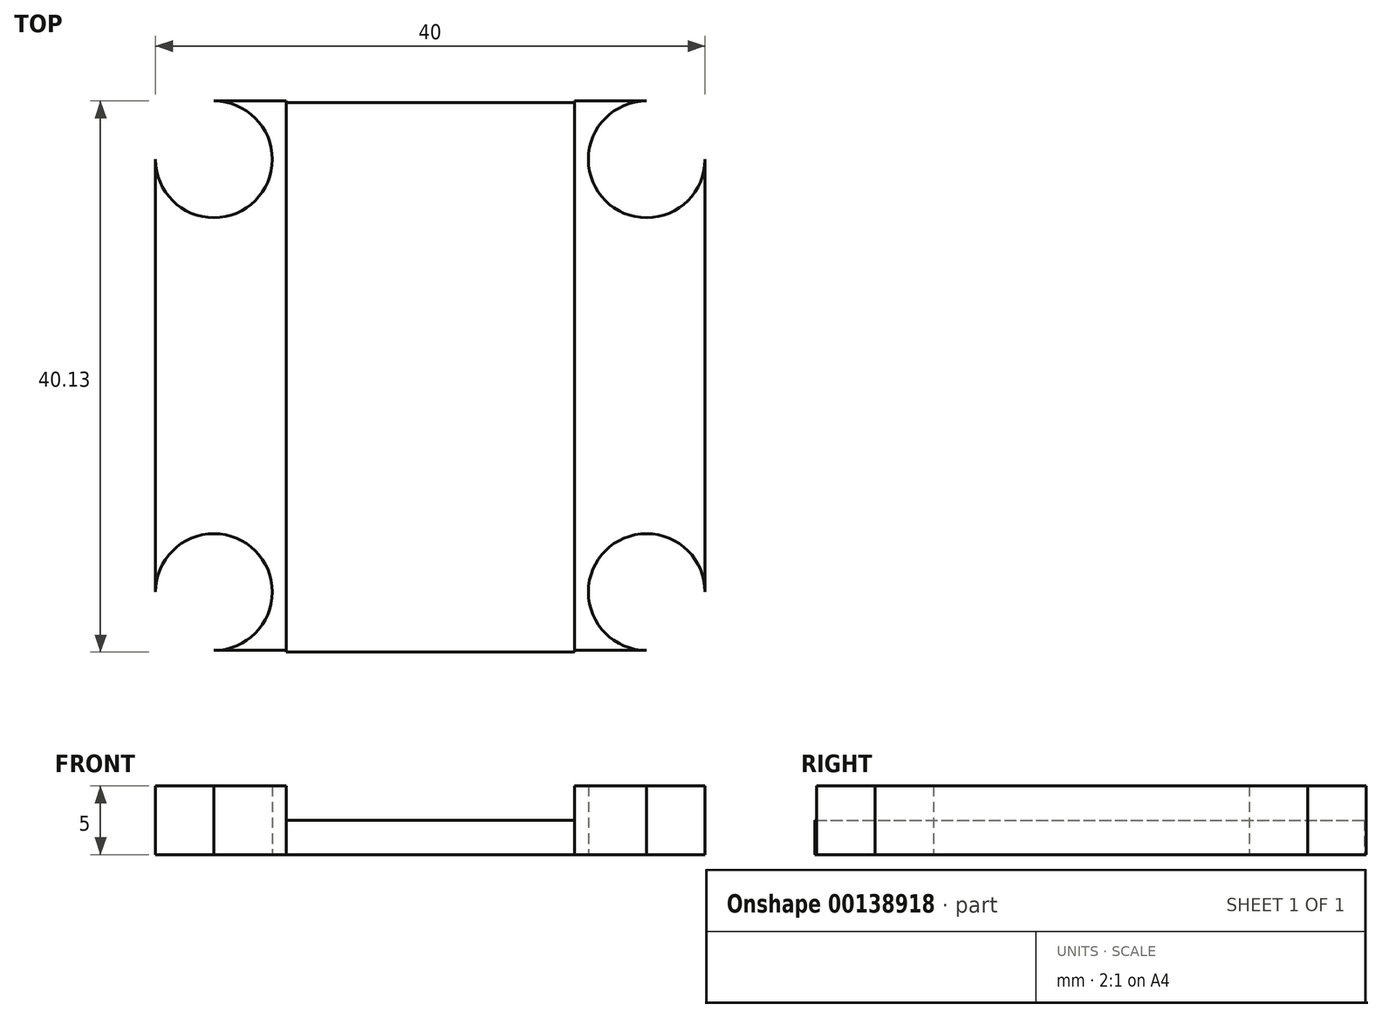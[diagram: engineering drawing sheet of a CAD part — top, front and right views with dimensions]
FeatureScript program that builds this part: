
annotation { "Feature Type Name" : "Feature", "Feature Type Description" : "" }
export const myFeature = defineFeature(function(context is Context, id is Id, definition is map)
    precondition{}
    {
        {
            var Q0;
            Q0=qCreatedBy(makeId("Top.planeOp"),FACE);
            var sketch = newSketch(context, id + "F0", { "sketchPlane" : qUnion([Q0])});
            skLineSegment(sketch, "E0.bottom", {"start": v(-32, 20.8) * mm, "end": v(8, 20.8) * mm});
            skLineSegment(sketch, "E0.top", {"start": v(-32, -19.2) * mm, "end": v(8, -19.2) * mm});
            skLineSegment(sketch, "E0.left", {"start": v(-32, 20.8) * mm, "end": v(-32, -19.2) * mm});
            skLineSegment(sketch, "E0.right", {"start": v(8, 20.8) * mm, "end": v(8, -19.2) * mm});
            skCircle(sketch, "E1", {"center": v(3.74, 16.55) * mm, "radius": 4.25 * mm});
            skCircle(sketch, "E2", {"center": v(-27.76, 16.55) * mm, "radius": 4.25 * mm});
            skCircle(sketch, "E3", {"center": v(3.74, -14.95) * mm, "radius": 4.25 * mm});
            skCircle(sketch, "E4", {"center": v(-27.76, -14.95) * mm, "radius": 4.25 * mm});
            skCircle(sketch, "E5", {"center": v(3.74, 16.55) * mm, "radius": 3.8 * mm});
            skCircle(sketch, "E6", {"center": v(3.74, -14.95) * mm, "radius": 3.8 * mm});
            skCircle(sketch, "E7", {"center": v(-27.76, 16.55) * mm, "radius": 3.8 * mm});
            skCircle(sketch, "E8", {"center": v(-27.76, -14.95) * mm, "radius": 3.8 * mm});
            skLineSegment(sketch, "E9.bottom", {"start": v(-22.5, -19.2) * mm, "end": v(-1.5, -19.2) * mm});
            skLineSegment(sketch, "E9.top", {"start": v(-22.5, 20.8) * mm, "end": v(-1.5, 20.8) * mm});
            skLineSegment(sketch, "E9.left", {"start": v(-22.5, -19.2) * mm, "end": v(-22.5, 20.8) * mm});
            skLineSegment(sketch, "E9.right", {"start": v(-1.5, -19.2) * mm, "end": v(-1.5, 20.8) * mm});
            skSolve(sketch);
        }
        {
            var Q0;
            {var subQ5=sQuery(id+"F0.wireOp",EDGE,"E9.left");Q0=makeQuery(id+"F0.imprint","IMPRINT",FACE,{"disambiguationData":[TD([[makeQuery(id+"F0.imprint","IMPRINT",EDGE,{"derivedFrom":subQ5}),1.0]])]});}
            var Q1;
            {var subQ7=sQuery(id+"F0.wireOp",EDGE,"E9.right");Q1=makeQuery(id+"F0.imprint","IMPRINT",FACE,{"disambiguationData":[TD([[makeQuery(id+"F0.imprint","IMPRINT",EDGE,{"derivedFrom":subQ7}),-1.0]])]});}
            extrude(context, id + "F1", {"entities" : qUnion([Q0, Q1]), "depth" : 5 * mm});
        }
        {
            var Q0;
            Q0=qCreatedBy(makeId("Top.planeOp"),FACE);
            var sketch = newSketch(context, id + "F2", { "sketchPlane" : qUnion([Q0])});
            skLineSegment(sketch, "E10.bottom", {"start": v(-1.5, -19.33) * mm, "end": v(-22.5, -19.33) * mm});
            skLineSegment(sketch, "E10.top", {"start": v(-1.5, 20.67) * mm, "end": v(-22.5, 20.67) * mm});
            skLineSegment(sketch, "E10.left", {"start": v(-1.5, -19.33) * mm, "end": v(-1.5, 20.67) * mm});
            skLineSegment(sketch, "E10.right", {"start": v(-22.5, -19.33) * mm, "end": v(-22.5, 20.67) * mm});
            skSolve(sketch);
        }
        {
            var Q0;
            Q0=makeQuery(id+"F2.imprint","IMPRINT",FACE,{"disambiguationData":[TD([[makeQuery(id+"F2.imprint","IMPRINT",EDGE,{"derivedFrom":sQuery(id+"F2.wireOp",EDGE,"E10.bottom")}),-1.0]])]});
            extrude(context, id + "F3", {"entities" : qUnion([Q0]), "depth" : 2.5 * mm});
        }
    });
